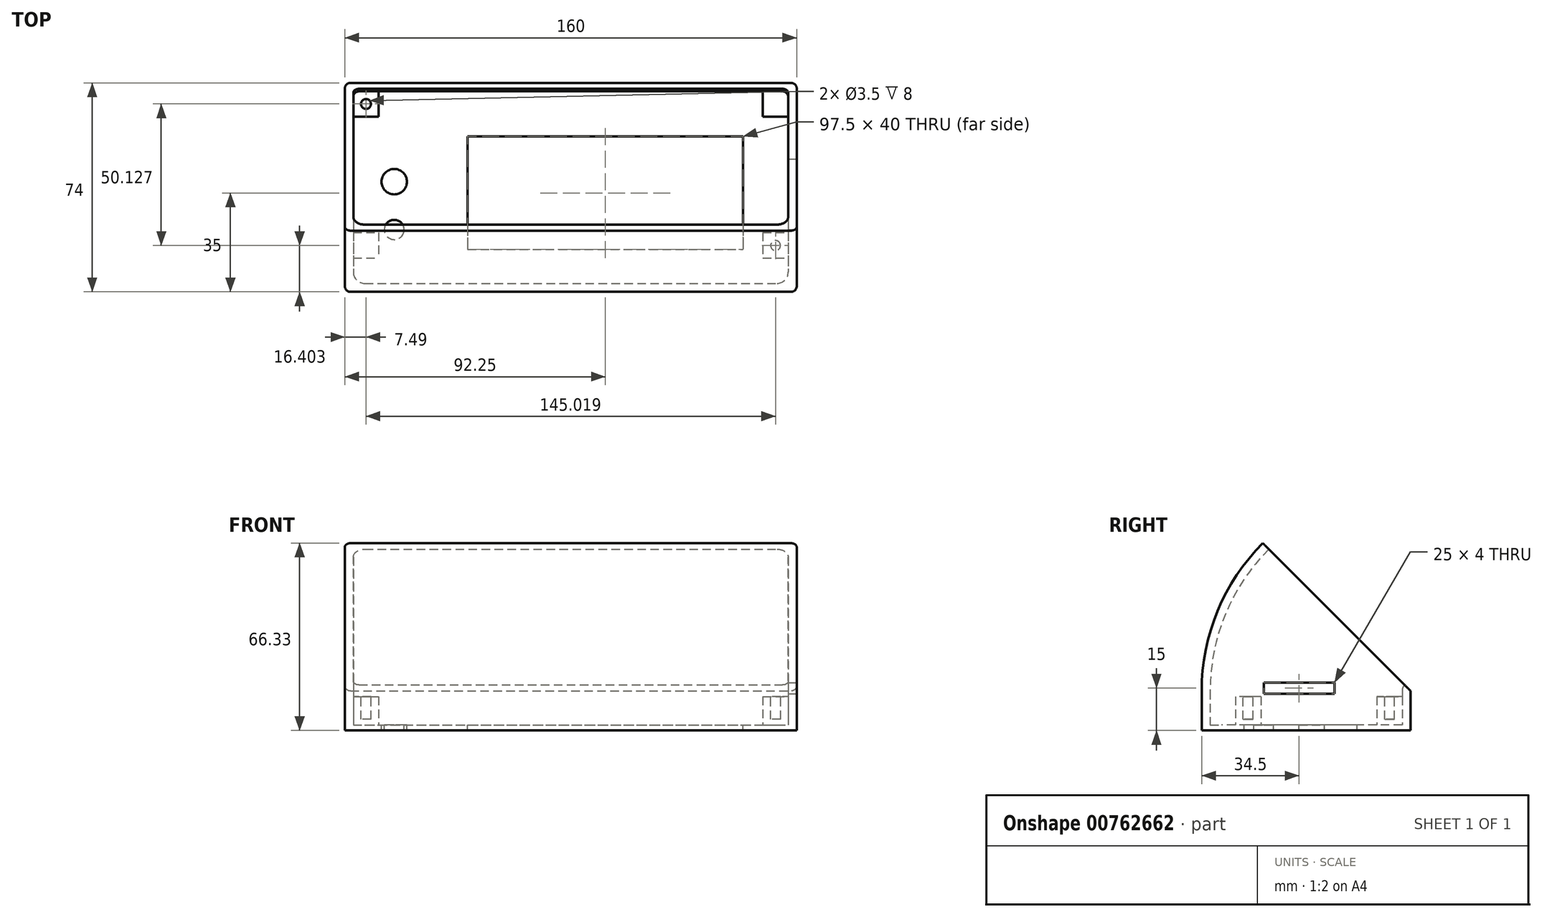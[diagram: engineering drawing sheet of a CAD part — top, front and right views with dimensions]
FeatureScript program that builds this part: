
annotation { "Feature Type Name" : "Feature", "Feature Type Description" : "" }
export const myFeature = defineFeature(function(context is Context, id is Id, definition is map)
    precondition{}
    {
        {
            var Q0;
            Q0=qCreatedBy(makeId("Top.planeOp"),FACE);
            var sketch = newSketch(context, id + "F0", { "sketchPlane" : qUnion([Q0])});
            skLineSegment(sketch, "E0.bottom", {"start": v(-80, 37) * mm, "end": v(80, 37) * mm});
            skLineSegment(sketch, "E0.top", {"start": v(-80, -37) * mm, "end": v(80, -37) * mm});
            skLineSegment(sketch, "E0.left", {"start": v(-80, 37) * mm, "end": v(-80, -37) * mm});
            skLineSegment(sketch, "E0.right", {"start": v(80, 37) * mm, "end": v(80, -37) * mm});
            skPoint(sketch, "E0.middle", {"position": v(0, 0) * mm});
            skSolve(sketch);
        }
        {
            var Q0;
            Q0=makeQuery(id+"F0.imprint","IMPRINT",FACE,{"disambiguationData":[TD([[makeQuery(id+"F0.imprint","IMPRINT",EDGE,{"derivedFrom":sQuery(id+"F0.wireOp",EDGE,"E0.bottom")}),-1.0]])]});
            var Q1;
            Q1 = qSketchRegion(id + "FPfe01AZxo6bJyg_1", true);
            extrude(context, id + "F1", {"entities" : qUnion([Q0, Q1]), "depth" : 2 * mm, "offsetDistance" : 25 * mm});
        }
        {
            var Q0;
            Q0=makeQuery(id+"F1.opExtrude","CAP_FACE",FACE,{"disambiguationData":[OSD([sQuery(id+"F0.wireOp",EDGE,"E0.bottom"),sQuery(id+"F0.wireOp",EDGE,"E0.top"),sQuery(id+"F0.wireOp",EDGE,"E0.left"),sQuery(id+"F0.wireOp",EDGE,"E0.right")])],"isStart":false});
            var sketch = newSketch(context, id + "F2", { "sketchPlane" : qUnion([Q0])});
            skLineSegment(sketch, "E1.bottom", {"start": v(-75, 32) * mm, "end": v(75, 32) * mm, "construction": true});
            skLineSegment(sketch, "E1.top", {"start": v(-75, -32) * mm, "end": v(75, -32) * mm, "construction": true});
            skLineSegment(sketch, "E1.left", {"start": v(-75, 32) * mm, "end": v(-75, -32) * mm, "construction": true});
            skLineSegment(sketch, "E1.right", {"start": v(75, 32) * mm, "end": v(75, -32) * mm, "construction": true});
            skPoint(sketch, "E1.middle", {"position": v(0, 0) * mm});
            skLineSegment(sketch, "E2.bottom", {"start": v(-36.5, 18) * mm, "end": v(61, 18) * mm});
            skLineSegment(sketch, "E2.top", {"start": v(-36.5, -22) * mm, "end": v(61, -22) * mm});
            skLineSegment(sketch, "E2.left", {"start": v(-36.5, 18) * mm, "end": v(-36.5, -22) * mm});
            skLineSegment(sketch, "E2.right", {"start": v(61, 18) * mm, "end": v(61, -22) * mm});
            skCircle(sketch, "E3", {"center": v(-62.5, 2) * mm, "radius": 4.5 * mm});
            skCircle(sketch, "E4", {"center": v(-62.5, -15) * mm, "radius": 3.5 * mm});
            skLineSegment(sketch, "E5", {"start": v(-62.5, 24.67) * mm, "end": v(-62.5, -18.28) * mm, "construction": true});
            skSolve(sketch);
        }
        {
            var Q0;
            Q0=makeQuery(id+"F2.imprint","IMPRINT",FACE,{"disambiguationData":[TD([[makeQuery(id+"F2.imprint","IMPRINT",EDGE,{"derivedFrom":sQuery(id+"F2.wireOp",EDGE,"E2.bottom")}),-1.0]])]});
            var Q1;
            Q1=makeQuery(id+"F2.imprint","IMPRINT",FACE,{"disambiguationData":[TD([[makeQuery(id+"F2.imprint","IMPRINT",EDGE,{"derivedFrom":sQuery(id+"F2.wireOp",EDGE,"E3")}),1.0]])]});
            var Q2;
            Q2=makeQuery(id+"F2.imprint","IMPRINT",FACE,{"disambiguationData":[TD([[makeQuery(id+"F2.imprint","IMPRINT",EDGE,{"derivedFrom":sQuery(id+"F2.wireOp",EDGE,"E4")}),1.0]])]});
            extrude(context, id + "F3", {"entities" : qUnion([Q0, Q1, Q2]), "operationType" : NewBodyOperationType.REMOVE, "oppositeDirection" : true, "depth" : 2 * mm, "offsetDistance" : 25 * mm});
        }
        {
            var Q0;
            Q0=makeQuery(id+"F1.opExtrude","CAP_FACE",FACE,{"disambiguationData":[OSD([sQuery(id+"F0.wireOp",EDGE,"E0.bottom"),sQuery(id+"F0.wireOp",EDGE,"E0.top"),sQuery(id+"F0.wireOp",EDGE,"E0.left"),sQuery(id+"F0.wireOp",EDGE,"E0.right")])],"isStart":false});
            var sketch = newSketch(context, id + "F4", { "sketchPlane" : qUnion([Q0])});
            skLineSegment(sketch, "E6", {"start": v(-72.5, 38) * mm, "end": v(-72.5, -30.27) * mm, "construction": true});
            skLineSegment(sketch, "E7", {"start": v(-81.28, 29.5) * mm, "end": v(-64.89, 29.5) * mm, "construction": true});
            skLineSegment(sketch, "E8", {"start": v(72.5, 36.84) * mm, "end": v(72.5, -28.65) * mm, "construction": true});
            skLineSegment(sketch, "E9", {"start": v(67.8, 29.5) * mm, "end": v(82.1, 29.5) * mm, "construction": true});
            skLineSegment(sketch, "E10.bottom", {"start": v(-77, 25) * mm, "end": v(-68, 25) * mm});
            skLineSegment(sketch, "E10.top", {"start": v(-77, 34) * mm, "end": v(-68, 34) * mm});
            skLineSegment(sketch, "E10.left", {"start": v(-77, 25) * mm, "end": v(-77, 34) * mm});
            skLineSegment(sketch, "E10.right", {"start": v(-68, 25) * mm, "end": v(-68, 34) * mm});
            skPoint(sketch, "E10.middle", {"position": v(-72.5, 29.5) * mm});
            skLineSegment(sketch, "E11.bottom", {"start": v(68, 34) * mm, "end": v(77, 34) * mm});
            skLineSegment(sketch, "E11.top", {"start": v(68, 25) * mm, "end": v(77, 25) * mm});
            skLineSegment(sketch, "E11.left", {"start": v(68, 34) * mm, "end": v(68, 25) * mm});
            skLineSegment(sketch, "E11.right", {"start": v(77, 34) * mm, "end": v(77, 25) * mm});
            skPoint(sketch, "E11.middle", {"position": v(72.5, 29.5) * mm});
            skLineSegment(sketch, "E12", {"start": v(-84.1, -20.5) * mm, "end": v(84.4, -20.5) * mm, "construction": true});
            skLineSegment(sketch, "E13.bottom", {"start": v(-77, -16) * mm, "end": v(-68, -16) * mm});
            skLineSegment(sketch, "E13.top", {"start": v(-77, -25) * mm, "end": v(-68, -25) * mm});
            skLineSegment(sketch, "E13.left", {"start": v(-77, -16) * mm, "end": v(-77, -25) * mm});
            skLineSegment(sketch, "E13.right", {"start": v(-68, -16) * mm, "end": v(-68, -25) * mm});
            skPoint(sketch, "E13.middle", {"position": v(-72.5, -20.5) * mm});
            skLineSegment(sketch, "E14.bottom", {"start": v(68, -16) * mm, "end": v(77, -16) * mm});
            skLineSegment(sketch, "E14.top", {"start": v(68, -25) * mm, "end": v(77, -25) * mm});
            skLineSegment(sketch, "E14.left", {"start": v(68, -16) * mm, "end": v(68, -25) * mm});
            skLineSegment(sketch, "E14.right", {"start": v(77, -16) * mm, "end": v(77, -25) * mm});
            skPoint(sketch, "E14.middle", {"position": v(72.5, -20.5) * mm});
            skSolve(sketch);
        }
        {
            var Q0;
            Q0=makeQuery(id+"F4.imprint","IMPRINT",FACE,{"disambiguationData":[TD([[makeQuery(id+"F4.imprint","IMPRINT",EDGE,{"derivedFrom":sQuery(id+"F4.wireOp",EDGE,"E11.bottom")}),-1.0]])]});
            var Q1;
            Q1=makeQuery(id+"F4.imprint","IMPRINT",FACE,{"disambiguationData":[TD([[makeQuery(id+"F4.imprint","IMPRINT",EDGE,{"derivedFrom":sQuery(id+"F4.wireOp",EDGE,"E10.bottom")}),1.0]])]});
            var Q2;
            Q2=makeQuery(id+"F4.imprint","IMPRINT",FACE,{"disambiguationData":[TD([[makeQuery(id+"F4.imprint","IMPRINT",EDGE,{"derivedFrom":sQuery(id+"F4.wireOp",EDGE,"E13.bottom")}),-1.0]])]});
            var Q3;
            Q3=makeQuery(id+"F4.imprint","IMPRINT",FACE,{"disambiguationData":[TD([[makeQuery(id+"F4.imprint","IMPRINT",EDGE,{"derivedFrom":sQuery(id+"F4.wireOp",EDGE,"E14.bottom")}),-1.0]])]});
            extrude(context, id + "F5", {"entities" : qUnion([Q0, Q1, Q2, Q3]), "operationType" : NewBodyOperationType.ADD, "depth" : 10 * mm, "offsetDistance" : 25 * mm});
        }
        {
            var Q0;
            Q0=makeQuery(id+"F5.opExtrude","CAP_FACE",FACE,{"disambiguationData":[OSD([sQuery(id+"F4.wireOp",EDGE,"E10.bottom"),sQuery(id+"F4.wireOp",EDGE,"E10.top"),sQuery(id+"F4.wireOp",EDGE,"E10.left"),sQuery(id+"F4.wireOp",EDGE,"E10.right")])],"isStart":false});
            var sketch = newSketch(context, id + "F6", { "sketchPlane" : qUnion([Q0])});
            skCircle(sketch, "E15", {"center": v(-72.5, 29.53) * mm, "radius": 1.75 * mm});
            skCircle(sketch, "E16.MirrorC", {"center": v(72.5, 29.53) * mm, "radius": 1.75 * mm});
            skCircle(sketch, "E17.MirrorC", {"center": v(-72.5, -20.6) * mm, "radius": 1.75 * mm});
            skCircle(sketch, "E18.MirrorC", {"center": v(72.5, -20.6) * mm, "radius": 1.75 * mm});
            skSolve(sketch);
        }
        {
            var Q0;
            Q0=makeQuery(id+"F6.imprint","IMPRINT",FACE,{"disambiguationData":[TD([[makeQuery(id+"F6.imprint","IMPRINT",EDGE,{"derivedFrom":sQuery(id+"F6.wireOp",EDGE,"E15")}),1.0]])]});
            var Q1;
            Q1=makeQuery(id+"F6.imprint","IMPRINT",FACE,{"disambiguationData":[TD([[makeQuery(id+"F6.imprint","IMPRINT",EDGE,{"derivedFrom":sQuery(id+"F6.wireOp",EDGE,"E17.MirrorC")}),-1.0]])]});
            var Q2;
            Q2=makeQuery(id+"F6.imprint","IMPRINT",FACE,{"disambiguationData":[TD([[makeQuery(id+"F6.imprint","IMPRINT",EDGE,{"derivedFrom":sQuery(id+"F6.wireOp",EDGE,"E16.MirrorC")}),-1.0]])]});
            var Q3;
            Q3=makeQuery(id+"F6.imprint","IMPRINT",FACE,{"disambiguationData":[TD([[makeQuery(id+"F6.imprint","IMPRINT",EDGE,{"derivedFrom":sQuery(id+"F6.wireOp",EDGE,"E18.MirrorC")}),1.0]])]});
            extrude(context, id + "F7", {"entities" : qUnion([Q0, Q1, Q2, Q3]), "operationType" : NewBodyOperationType.REMOVE, "oppositeDirection" : true, "depth" : 8 * mm, "offsetDistance" : 25 * mm});
        }
        {
            var Q0;
            Q0=makeQuery(id+"F1.opExtrude","CAP_FACE",FACE,{"disambiguationData":[OSD([sQuery(id+"F0.wireOp",EDGE,"E0.bottom"),sQuery(id+"F0.wireOp",EDGE,"E0.top"),sQuery(id+"F0.wireOp",EDGE,"E0.left"),sQuery(id+"F0.wireOp",EDGE,"E0.right")])],"isStart":false});
            var sketch = newSketch(context, id + "F8", { "sketchPlane" : qUnion([Q0])});
            skLineSegment(sketch, "E19.bottom", {"start": v(-80, 37) * mm, "end": v(80, 37) * mm});
            skLineSegment(sketch, "E19.top", {"start": v(-80, -37) * mm, "end": v(80, -37) * mm});
            skLineSegment(sketch, "E19.left", {"start": v(-80, 37) * mm, "end": v(-80, -37) * mm});
            skLineSegment(sketch, "E19.right", {"start": v(80, 37) * mm, "end": v(80, -37) * mm});
            skPoint(sketch, "E19.middle", {"position": v(0, 0) * mm});
            skLineSegment(sketch, "E20.bottom", {"start": v(-77, 34) * mm, "end": v(77, 34) * mm});
            skLineSegment(sketch, "E20.top", {"start": v(-77, -34) * mm, "end": v(77, -34) * mm});
            skLineSegment(sketch, "E20.left", {"start": v(-77, 34) * mm, "end": v(-77, -34) * mm});
            skLineSegment(sketch, "E20.right", {"start": v(77, 34) * mm, "end": v(77, -34) * mm});
            skSolve(sketch);
        }
        {
            var Q0;
            Q0=makeQuery(id+"F8.imprint","IMPRINT",FACE,{"disambiguationData":[TD([[makeQuery(id+"F8.imprint","IMPRINT",EDGE,{"derivedFrom":sQuery(id+"F8.wireOp",EDGE,"E19.bottom")}),-1.0]])]});
            extrude(context, id + "F9", {"entities" : qUnion([Q0]), "operationType" : NewBodyOperationType.ADD, "depth" : 12 * mm, "offsetDistance" : 25 * mm});
        }
        {
            var Q0;
            Q0=makeQuery(id+"F9.opExtrude","CAP_FACE",FACE,{"disambiguationData":[OSD([sQuery(id+"F8.wireOp",EDGE,"E19.bottom"),sQuery(id+"F8.wireOp",EDGE,"E19.top"),sQuery(id+"F8.wireOp",EDGE,"E19.left"),sQuery(id+"F8.wireOp",EDGE,"E19.right"),sQuery(id+"F8.wireOp",EDGE,"E20.bottom"),sQuery(id+"F8.wireOp",EDGE,"E20.top"),sQuery(id+"F8.wireOp",EDGE,"E20.left"),sQuery(id+"F8.wireOp",EDGE,"E20.right")])],"isStart":false});
            var Q1;
            Q1=makeQuery(id+"F9.opExtrude","CAP_EDGE",EDGE,{"disambiguationData":[OSD([sQuery(id+"F8.wireOp",EDGE,"E19.bottom")])],"isStart":false});
            revolve(context, id + "F10", {"operationType" : NewBodyOperationType.ADD, "surfaceOperationType" : NewSurfaceOperationType.NEW, "entities" : qUnion([Q0]), "axis" : qUnion([Q1]), "revolveType" : RevolveType.ONE_DIRECTION, "oppositeDirection" : true, "angle" : 45 * degree});
        }
        {
            var Q0;
            {var subQ0=sQuery(id+"F8.wireOp",EDGE,"E19.right");Q0=makeQuery(id+"F10.boolean.opBoolean","MERGE",FACE,{"derivedFrom":[makeQuery(id+"F9.boolean.opBoolean","MERGE",FACE,{"derivedFrom":[makeQuery(id+"F1.opExtrude","SWEPT_FACE",FACE,{"disambiguationData":[OSD([sQuery(id+"F0.wireOp",EDGE,"E0.right")])]}),makeQuery(id+"F9.opExtrude","SWEPT_FACE",FACE,{"disambiguationData":[OSD([subQ0])]})]}),makeQuery(id+"F10.opRevolve","SWEPT_FACE",FACE,{"disambiguationData":[OSD([subQ0])]})]});}
            var sketch = newSketch(context, id + "F11", { "sketchPlane" : qUnion([Q0])});
            skLineSegment(sketch, "E21.bottom", {"start": v(10, 17) * mm, "end": v(-15, 17) * mm});
            skLineSegment(sketch, "E21.top", {"start": v(10, 13) * mm, "end": v(-15, 13) * mm});
            skLineSegment(sketch, "E21.left", {"start": v(10, 17) * mm, "end": v(10, 13) * mm});
            skLineSegment(sketch, "E21.right", {"start": v(-15, 17) * mm, "end": v(-15, 13) * mm});
            skSolve(sketch);
        }
        {
            var Q0;
            Q0=makeQuery(id+"F11.imprint","IMPRINT",FACE,{"disambiguationData":[TD([[makeQuery(id+"F11.imprint","IMPRINT",EDGE,{"derivedFrom":sQuery(id+"F11.wireOp",EDGE,"E21.bottom")}),1.0]])]});
            extrude(context, id + "F12", {"entities" : qUnion([Q0]), "operationType" : NewBodyOperationType.REMOVE, "oppositeDirection" : true, "depth" : 3 * mm, "offsetDistance" : 25 * mm});
        }
        {
            var Q0;
            Q0=makeQuery(id+"F9.boolean.opBoolean","MERGE",EDGE,{"derivedFrom":[makeQuery(id+"F1.opExtrude","SWEPT_EDGE",EDGE,{"disambiguationData":[OSD([sQuery(id+"F0.wireOp",EDGE,"E0.bottom"),sQuery(id+"F0.wireOp",EDGE,"E0.right")])]}),makeQuery(id+"F9.opExtrude","SWEPT_EDGE",EDGE,{"disambiguationData":[OSD([sQuery(id+"F8.wireOp",EDGE,"E19.bottom"),sQuery(id+"F8.wireOp",EDGE,"E19.right")])]})]});
            var Q1;
            Q1=makeQuery(id+"F10.opRevolve","SWEPT_EDGE",EDGE,{"disambiguationData":[OSD([sQuery(id+"F8.wireOp",EDGE,"E19.top"),sQuery(id+"F8.wireOp",EDGE,"E19.right")])]});
            var Q2;
            Q2=makeQuery(id+"F9.boolean.opBoolean","MERGE",EDGE,{"derivedFrom":[makeQuery(id+"F1.opExtrude","SWEPT_EDGE",EDGE,{"disambiguationData":[OSD([sQuery(id+"F0.wireOp",EDGE,"E0.top"),sQuery(id+"F0.wireOp",EDGE,"E0.right")])]}),makeQuery(id+"F9.opExtrude","SWEPT_EDGE",EDGE,{"disambiguationData":[OSD([sQuery(id+"F8.wireOp",EDGE,"E19.top"),sQuery(id+"F8.wireOp",EDGE,"E19.right")])]})]});
            var Q3;
            Q3=makeQuery(id+"F9.boolean.opBoolean","MERGE",EDGE,{"derivedFrom":[makeQuery(id+"F1.opExtrude","SWEPT_EDGE",EDGE,{"disambiguationData":[OSD([sQuery(id+"F0.wireOp",EDGE,"E0.bottom"),sQuery(id+"F0.wireOp",EDGE,"E0.left")])]}),makeQuery(id+"F9.opExtrude","SWEPT_EDGE",EDGE,{"disambiguationData":[OSD([sQuery(id+"F8.wireOp",EDGE,"E19.bottom"),sQuery(id+"F8.wireOp",EDGE,"E19.left")])]})]});
            var Q4;
            Q4=makeQuery(id+"F10.opRevolve","SWEPT_EDGE",EDGE,{"disambiguationData":[OSD([sQuery(id+"F8.wireOp",EDGE,"E19.top"),sQuery(id+"F8.wireOp",EDGE,"E19.left")])]});
            var Q5;
            Q5=makeQuery(id+"F9.boolean.opBoolean","MERGE",EDGE,{"derivedFrom":[makeQuery(id+"F1.opExtrude","SWEPT_EDGE",EDGE,{"disambiguationData":[OSD([sQuery(id+"F0.wireOp",EDGE,"E0.top"),sQuery(id+"F0.wireOp",EDGE,"E0.left")])]}),makeQuery(id+"F9.opExtrude","SWEPT_EDGE",EDGE,{"disambiguationData":[OSD([sQuery(id+"F8.wireOp",EDGE,"E19.top"),sQuery(id+"F8.wireOp",EDGE,"E19.left")])]})]});
            var Q6;
            Q6=makeQuery(id+"F10.opRevolve","SWEPT_EDGE",EDGE,{"disambiguationData":[OSD([sQuery(id+"F8.wireOp",EDGE,"E20.bottom"),sQuery(id+"F8.wireOp",EDGE,"E20.left")])]});
            var Q7;
            Q7=makeQuery(id+"F10.opRevolve","SWEPT_EDGE",EDGE,{"disambiguationData":[OSD([sQuery(id+"F8.wireOp",EDGE,"E20.bottom"),sQuery(id+"F8.wireOp",EDGE,"E20.right")])]});
            fillet(context, id + "F13", {"entities" : qUnion([Q0, Q1, Q2, Q3, Q4, Q5, Q6, Q7]), "radius" : 2 * mm, "tangentPropagation" : true, "allowEdgeOverflow" : false});
        }
        {
            var Q0;
            Q0=makeQuery(id+"F10.opRevolve","SWEPT_EDGE",EDGE,{"disambiguationData":[OSD([sQuery(id+"F8.wireOp",EDGE,"E20.top"),sQuery(id+"F8.wireOp",EDGE,"E20.left")])]});
            var Q1;
            Q1=makeQuery(id+"F10.opRevolve","SWEPT_EDGE",EDGE,{"disambiguationData":[OSD([sQuery(id+"F8.wireOp",EDGE,"E20.top"),sQuery(id+"F8.wireOp",EDGE,"E20.right")])]});
            fillet(context, id + "F14", {"entities" : qUnion([Q0, Q1]), "radius" : 4 * mm, "tangentPropagation" : true, "allowEdgeOverflow" : false});
        }
    });
